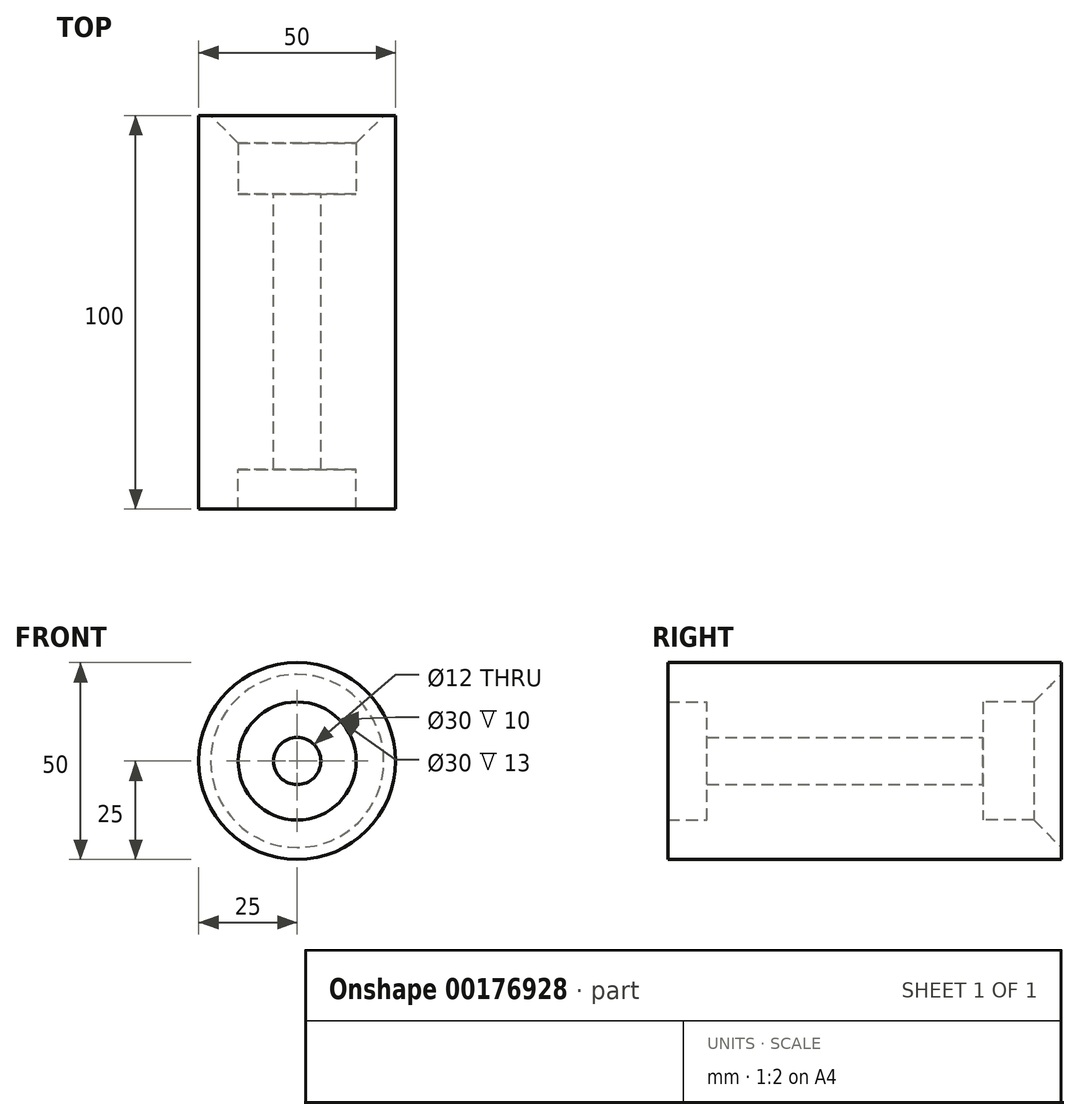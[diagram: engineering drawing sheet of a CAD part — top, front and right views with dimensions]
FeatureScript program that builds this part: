
annotation { "Feature Type Name" : "Feature", "Feature Type Description" : "" }
export const myFeature = defineFeature(function(context is Context, id is Id, definition is map)
    precondition{}
    {
        {
            var Q0;
            Q0=qCreatedBy(makeId("Front.planeOp"),FACE);
            var sketch = newSketch(context, id + "F0", { "sketchPlane" : qUnion([Q0])});
            skCircle(sketch, "E0", {"center": v(0, 0) * mm, "radius": 25 * mm});
            skCircle(sketch, "E1", {"center": v(0, 0) * mm, "radius": 6 * mm});
            skSolve(sketch);
        }
        {
            var Q0;
            Q0 = qSketchRegion(id + "F0", true);
            extrude(context, id + "F1", {"entities" : qUnion([Q0]), "depth" : 70 * mm});
        }
        {
            var Q0;
            Q0=makeQuery(id+"F1.opExtrude","CAP_FACE",FACE,{"disambiguationData":[OSD([sQuery(id+"F0.wireOp",EDGE,"E0"),sQuery(id+"F0.wireOp",EDGE,"E1")])],"isStart":false});
            var sketch = newSketch(context, id + "F2", { "sketchPlane" : qUnion([Q0])});
            skCircle(sketch, "E2", {"center": v(0, 0) * mm, "radius": 15 * mm});
            skSolve(sketch);
        }
        {
            var Q0;
            Q0=makeQuery(id+"F2.imprint","IMPRINT",FACE,{"disambiguationData":[TD([[makeQuery(id+"F2.imprint","IMPRINT",EDGE,{"derivedFrom":sQuery(id+"F2.wireOp",EDGE,"E2")}),-1.0]])]});
            extrude(context, id + "F3", {"entities" : qUnion([Q0]), "operationType" : NewBodyOperationType.ADD, "depth" : 10 * mm});
        }
        {
            var Q0;
            Q0=makeQuery(id+"F1.opExtrude","CAP_FACE",FACE,{"disambiguationData":[OSD([sQuery(id+"F0.wireOp",EDGE,"E0"),sQuery(id+"F0.wireOp",EDGE,"E1")])],"isStart":true});
            var sketch = newSketch(context, id + "F4", { "sketchPlane" : qUnion([Q0])});
            skCircle(sketch, "E3", {"center": v(0, 0) * mm, "radius": 15 * mm});
            skSolve(sketch);
        }
        {
            var Q0;
            Q0=makeQuery(id+"F4.imprint","IMPRINT",FACE,{"disambiguationData":[TD([[makeQuery(id+"F4.imprint","IMPRINT",EDGE,{"derivedFrom":sQuery(id+"F4.wireOp",EDGE,"E3")}),-1.0]])]});
            extrude(context, id + "F5", {"entities" : qUnion([Q0]), "operationType" : NewBodyOperationType.ADD, "depth" : 20 * mm});
        }
        {
            var Q0;
            Q0=makeQuery(id+"F5.opExtrude","CAP_EDGE",EDGE,{"disambiguationData":[OSD([sQuery(id+"F4.wireOp",EDGE,"E3")])],"isStart":false});
            chamfer(context, id + "F6", {"entities" : qUnion([Q0]), "width" : 7 * mm, "tangentPropagation" : true});
        }
    });
